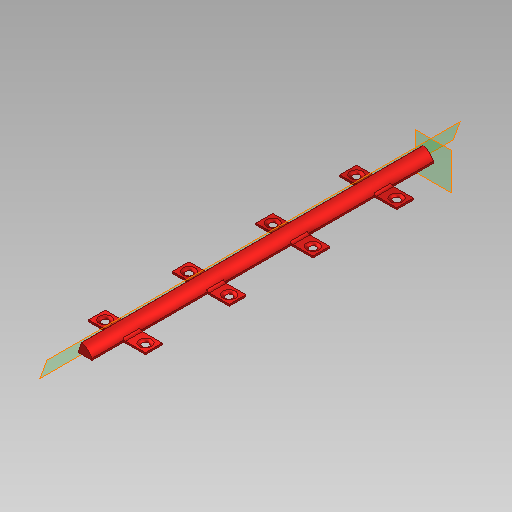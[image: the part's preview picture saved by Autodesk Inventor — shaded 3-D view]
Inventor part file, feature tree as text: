
AUTODESK INVENTOR PART (.ipt)
format: ipt  version: 2020 (Build 240168000, 168)  size: 299,008 bytes
history: native  units: in
note: dims shown in document units (in); Inventor stores cm internally (conversion verified against a paired STEP export)
features: sketch x7, extrude x5, fillet x3, plane x2, sweep x1, pattern_linear x1, mirror x1
ambient origin geometry x8: Origin, YZ Plane, XZ Plane, XY Plane, X Axis, Y Axis, Z Axis, Center Point
bodies: Body1 (feature_tree)
feature tree (20):
  sketch  "Sketch1"  dims[d0=0.315in d1=8.0315in]
  plane  "Work Plane1"
  sketch  "Sketch2"  dims[d2=0.1575in d3=7.874in]
  plane  "Work Plane2"
  sweep  "Sweep2"
  extrude  "Extrusion3"  Depth=7.874in
  extrude  "Extrusion4"  Depth=0.0197in
  extrude  "Extrusion5"  Depth=0.0197in
  extrude  "Extrusion6"  Depth=7.874in
  pattern_linear  "Rectangular Pattern2"  Spacing1=0.0394in  [1 undecoded]
  mirror  "Mirror1"
  fillet  "Fillet1"  Radius=0.0787in
  fillet  "Fillet2"  Radius=0.9843in
  fillet  "Fillet3"  Radius=0.5906in
  extrude  "Extrusion7"  Depth=0.5906in
  sketch  "Sketch3"  dims[d4=0.481in d5=0.0197in]
  sketch  "Sketch5"  dims[d6=0.1772in d7=0.0197in]
  sketch  "Sketch6"  dims[d8=8.0315in d10=7.874in]
  sketch  "Sketch7"  dims[d17=0.0in d18=0.0in]
  sketch  "Sketch8"  dims[d19=0.3937in d20=0.0in d21=0.0394in d22=0.0in d23=0.0787in d24=0.0in d25=0.9843in d26=0.5906in d27=0.5906in d28=0.5906in d29=0.0394in d30=0.3543in d31=0.1969in d32=0.1969in d33=0.1575in d34=0.0394in d35=0.0in d42=1.5748in d44=1.9685in d45=0.0748in d46=0.4724in d47=0.0157in d48=0.0394in d49=0.0in]
note: 1 required parameter value undecoded (feature->parameter linkage not recoverable at this tier; creation-order binding heuristic only, values carry confidence <= 0.55)
